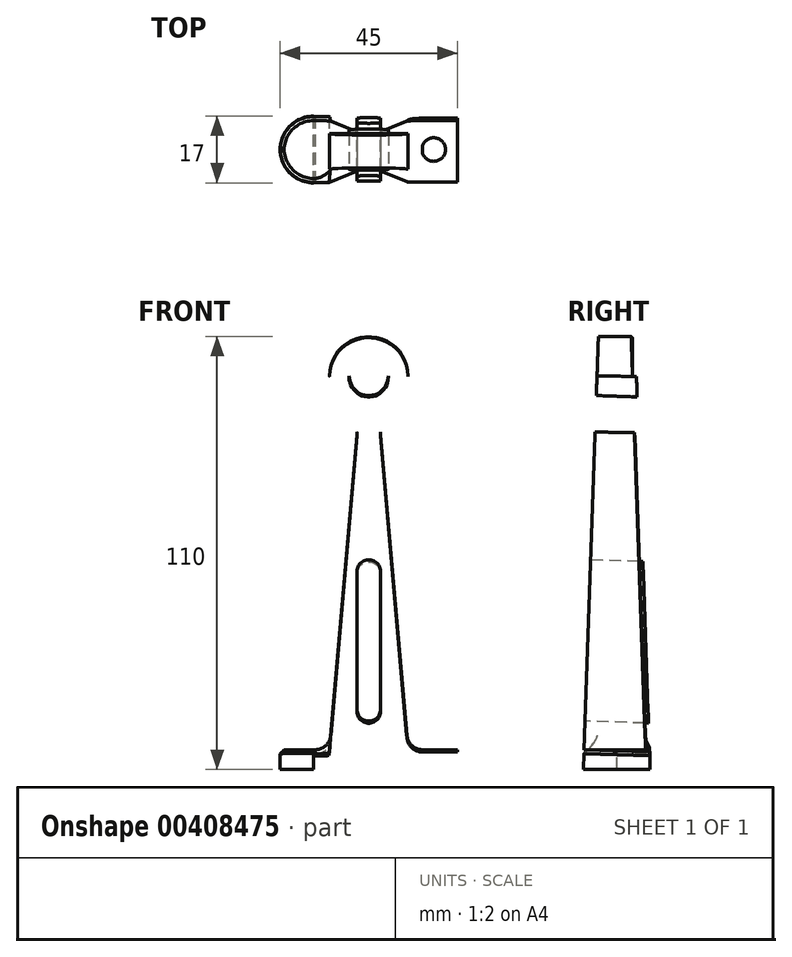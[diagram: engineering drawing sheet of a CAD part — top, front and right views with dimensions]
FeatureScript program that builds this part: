
annotation { "Feature Type Name" : "Feature", "Feature Type Description" : "" }
export const myFeature = defineFeature(function(context is Context, id is Id, definition is map)
    precondition{}
    {
        {
            var Q0;
            Q0=qCreatedBy(makeId("Front.planeOp"),FACE);
            var sketch = newSketch(context, id + "F0", { "sketchPlane" : qUnion([Q0])});
            skArc(sketch, "E0", {"start": v(6.1, 92.07) * mm, "mid": v(0, 110) * mm, "end": v(-6.1, 92.07) * mm});
            skArc(sketch, "E1", {"start": v(-7.5, 0) * mm, "mid": v(0, 7.5) * mm, "end": v(7.5, 0) * mm});
            skLineSegment(sketch, "E2", {"start": v(7.5, 0) * mm, "end": v(22.5, 0) * mm});
            skLineSegment(sketch, "E3", {"start": v(-7.5, 0) * mm, "end": v(-22.5, 0) * mm});
            skLineSegment(sketch, "E4", {"start": v(-22.5, 0) * mm, "end": v(-22.5, 5) * mm});
            skLineSegment(sketch, "E5", {"start": v(-22.5, 5) * mm, "end": v(-13.67, 5) * mm});
            skLineSegment(sketch, "E6", {"start": v(22.5, 0) * mm, "end": v(22.5, 5) * mm});
            skLineSegment(sketch, "E7", {"start": v(22.5, 5) * mm, "end": v(13.67, 5) * mm});
            skCircle(sketch, "E8", {"center": v(0, 100) * mm, "radius": 5 * mm});
            skArc(sketch, "E9", {"start": v(6.1, 92.07) * mm, "mid": v(3.65, 88.95) * mm, "end": v(3, 85.03) * mm});
            skArc(sketch, "E10", {"start": v(-6.1, 92.07) * mm, "mid": v(-3.65, 88.95) * mm, "end": v(-3, 85.03) * mm});
            skArc(sketch, "E11", {"start": v(9.68, 8.65) * mm, "mid": v(10.96, 6.05) * mm, "end": v(13.67, 5) * mm});
            skArc(sketch, "E12", {"start": v(-9.68, 8.65) * mm, "mid": v(-10.96, 6.05) * mm, "end": v(-13.67, 5) * mm});
            skLineSegment(sketch, "E13", {"start": v(-3, 85.03) * mm, "end": v(-9.68, 8.65) * mm});
            skLineSegment(sketch, "E14", {"start": v(3, 85.03) * mm, "end": v(9.68, 8.65) * mm});
            skSolve(sketch);
        }
        {
            var Q0;
            Q0 = qSketchRegion(id + "F0", true);
            extrude(context, id + "F1", {"entities" : qUnion([Q0]), "endBound" : BoundingType.SYMMETRIC, "depth" : 17 * mm});
        }
        {
            var Q0;
            Q0=makeQuery(id+"F1.opExtrude","SWEPT_FACE",FACE,{"disambiguationData":[OSD([sQuery(id+"F0.wireOp",EDGE,"E6")])]});
            var sketch = newSketch(context, id + "F2", { "sketchPlane" : qUnion([Q0])});
            skLineSegment(sketch, "E15", {"start": v(-8.5, 0) * mm, "end": v(-4.37, 118.17) * mm});
            skLineSegment(sketch, "E16", {"start": v(-4.37, 118.17) * mm, "end": v(-19.07, 118.17) * mm});
            skLineSegment(sketch, "E17", {"start": v(-19.07, 118.17) * mm, "end": v(-8.5, 0) * mm});
            skLineSegment(sketch, "E18", {"start": v(0, 0) * mm, "end": v(0, 114.36) * mm, "construction": true});
            skLineSegment(sketch, "E19.MirrorCS", {"start": v(4.37, 118.17) * mm, "end": v(19.07, 118.17) * mm});
            skLineSegment(sketch, "E20.MirrorCS", {"start": v(19.07, 118.17) * mm, "end": v(8.5, 0) * mm});
            skLineSegment(sketch, "E21.MirrorCS", {"start": v(8.5, 0) * mm, "end": v(4.37, 118.17) * mm});
            skSolve(sketch);
        }
        {
            var Q0;
            Q0 = qSketchRegion(id + "F2", true);
            extrude(context, id + "F3", {"entities" : qUnion([Q0]), "operationType" : NewBodyOperationType.REMOVE, "endBound" : BoundingType.THROUGH_ALL, "oppositeDirection" : true, "depth" : 25 * mm});
        }
        {
            var Q0;
            Q0=makeQuery(id+"F1.opExtrude","SWEPT_FACE",FACE,{"disambiguationData":[OSD([sQuery(id+"F0.wireOp",EDGE,"E7")])]});
            var sketch = newSketch(context, id + "F4", { "sketchPlane" : qUnion([Q0])});
            skCircle(sketch, "E22", {"center": v(16.5, 0) * mm, "radius": 3 * mm});
            skSolve(sketch);
        }
        {
            var Q0;
            {var subQ0=sQuery(id+"F4.wireOp",EDGE,"E22");var subQ1=makeQuery(id+"F1.opExtrude","SWEPT_EDGE",EDGE,{"disambiguationData":[OSD([sQuery(id+"F0.wireOp",EDGE,"E7"),sQuery(id+"F0.wireOp",EDGE,"E11")])]});var subQ2=makeQuery(id+"F4.imprint","INTERSECT",VERTEX,{"disambiguationData":[OD(0.0)],"derivedFrom":[subQ1,subQ0]});Q0=makeQuery(id+"F4.imprint","IMPRINT",FACE,{"disambiguationData":[TD([[makeQuery(id+"F4.imprint","IMPRINT",EDGE,{"disambiguationData":[TD([[subQ2,-1.0]])],"derivedFrom":subQ0}),1.0]])]});}
            extrude(context, id + "F5", {"entities" : qUnion([Q0]), "operationType" : NewBodyOperationType.REMOVE, "oppositeDirection" : true, "depth" : 25 * mm});
        }
        {
            var Q0;
            Q0=makeQuery(id+"F3.boolean.opBoolean","COPY",EDGE,{"derivedFrom":makeQuery(id+"F3.opExtrude","CAP_EDGE",EDGE,{"disambiguationData":[OSD([sQuery(id+"F2.wireOp",EDGE,"E21.MirrorCS")])],"isStart":true})});
            var Q1;
            Q1=makeQuery(id+"F3.boolean.opBoolean","COPY",EDGE,{"derivedFrom":makeQuery(id+"F3.opExtrude","CAP_EDGE",EDGE,{"disambiguationData":[OSD([sQuery(id+"F2.wireOp",EDGE,"E15")])],"isStart":true})});
            var Q2;
            Q2=makeQuery(id+"F3.boolean.opBoolean","INTERSECT",EDGE,{"derivedFrom":[makeQuery(id+"F1.opExtrude","SWEPT_FACE",FACE,{"disambiguationData":[OSD([sQuery(id+"F0.wireOp",EDGE,"E4")])]}),makeQuery(id+"F3.opExtrude","SWEPT_FACE",FACE,{"disambiguationData":[OSD([sQuery(id+"F2.wireOp",EDGE,"E15")])]})]});
            var Q3;
            Q3=makeQuery(id+"F3.boolean.opBoolean","INTERSECT",EDGE,{"derivedFrom":[makeQuery(id+"F1.opExtrude","SWEPT_FACE",FACE,{"disambiguationData":[OSD([sQuery(id+"F0.wireOp",EDGE,"E4")])]}),makeQuery(id+"F3.opExtrude","SWEPT_FACE",FACE,{"disambiguationData":[OSD([sQuery(id+"F2.wireOp",EDGE,"E21.MirrorCS")])]})]});
            fillet(context, id + "F6", {"entities" : qUnion([Q0, Q1, Q2, Q3]), "radius" : 8.5 * mm, "tangentPropagation" : true, "allowEdgeOverflow" : false});
        }
        {
            var Q0;
            Q0=makeQuery(id+"F6.opFillet","BLEND_EDGE",EDGE,{"blendedFrom":[makeQuery(id+"F3.boolean.opBoolean","COPY",EDGE,{"derivedFrom":makeQuery(id+"F3.opExtrude","CAP_EDGE",EDGE,{"disambiguationData":[OSD([sQuery(id+"F2.wireOp",EDGE,"E15")])],"isStart":true})}),makeQuery(id+"F1.opExtrude","SWEPT_FACE",FACE,{"disambiguationData":[OSD([sQuery(id+"F0.wireOp",EDGE,"E7")])]})],"blendedInto":[makeQuery(id+"F1.opExtrude","SWEPT_FACE",FACE,{"disambiguationData":[OSD([sQuery(id+"F0.wireOp",EDGE,"E7")])]})]});
            var Q1;
            Q1=makeQuery(id+"F3.boolean.opBoolean","INTERSECT",EDGE,{"derivedFrom":[makeQuery(id+"F1.opExtrude","SWEPT_FACE",FACE,{"disambiguationData":[OSD([sQuery(id+"F0.wireOp",EDGE,"E14")])]}),makeQuery(id+"F3.opExtrude","SWEPT_FACE",FACE,{"disambiguationData":[OSD([sQuery(id+"F2.wireOp",EDGE,"E21.MirrorCS")])]})]});
            chamfer(context, id + "F7", {"entities" : qUnion([Q0, Q1]), "chamferType" : ChamferType.TWO_OFFSETS, "width1" : 1 * mm, "oppositeDirection" : false, "width2" : 1 * mm, "tangentPropagation" : true});
        }
        {
            var Q0;
            Q0=makeQuery(id+"F3.boolean.opBoolean","COPY",FACE,{"derivedFrom":makeQuery(id+"F3.opExtrude","SWEPT_FACE",FACE,{"disambiguationData":[OSD([sQuery(id+"F2.wireOp",EDGE,"E15")])]})});
            var sketch = newSketch(context, id + "F8", { "sketchPlane" : qUnion([Q0])});
            skLineSegment(sketch, "E23", {"start": v(0, 50) * mm, "end": v(0, 15) * mm});
            skArc(sketch, "E24.0.startCap", {"start": v(-3, 50) * mm, "mid": v(0, 53) * mm, "end": v(3, 50) * mm});
            skArc(sketch, "E24.0.endCap", {"start": v(3, 15) * mm, "mid": v(0, 12) * mm, "end": v(-3, 15) * mm});
            skLineSegment(sketch, "E24.0.left", {"start": v(3, 50) * mm, "end": v(3, 15) * mm});
            skLineSegment(sketch, "E24.0.right", {"start": v(-3, 50) * mm, "end": v(-3, 15) * mm});
            skSolve(sketch);
        }
        {
            var Q0;
            Q0=makeQuery(id+"F8.imprint","IMPRINT",FACE,{"disambiguationData":[TD([[makeQuery(id+"F8.imprint","IMPRINT",EDGE,{"derivedFrom":sQuery(id+"F8.wireOp",EDGE,"E24.0.startCap")}),-1.0]])]});
            extrude(context, id + "F9", {"entities" : qUnion([Q0]), "operationType" : NewBodyOperationType.REMOVE, "oppositeDirection" : true, "depth" : 25 * mm});
        }
    });
